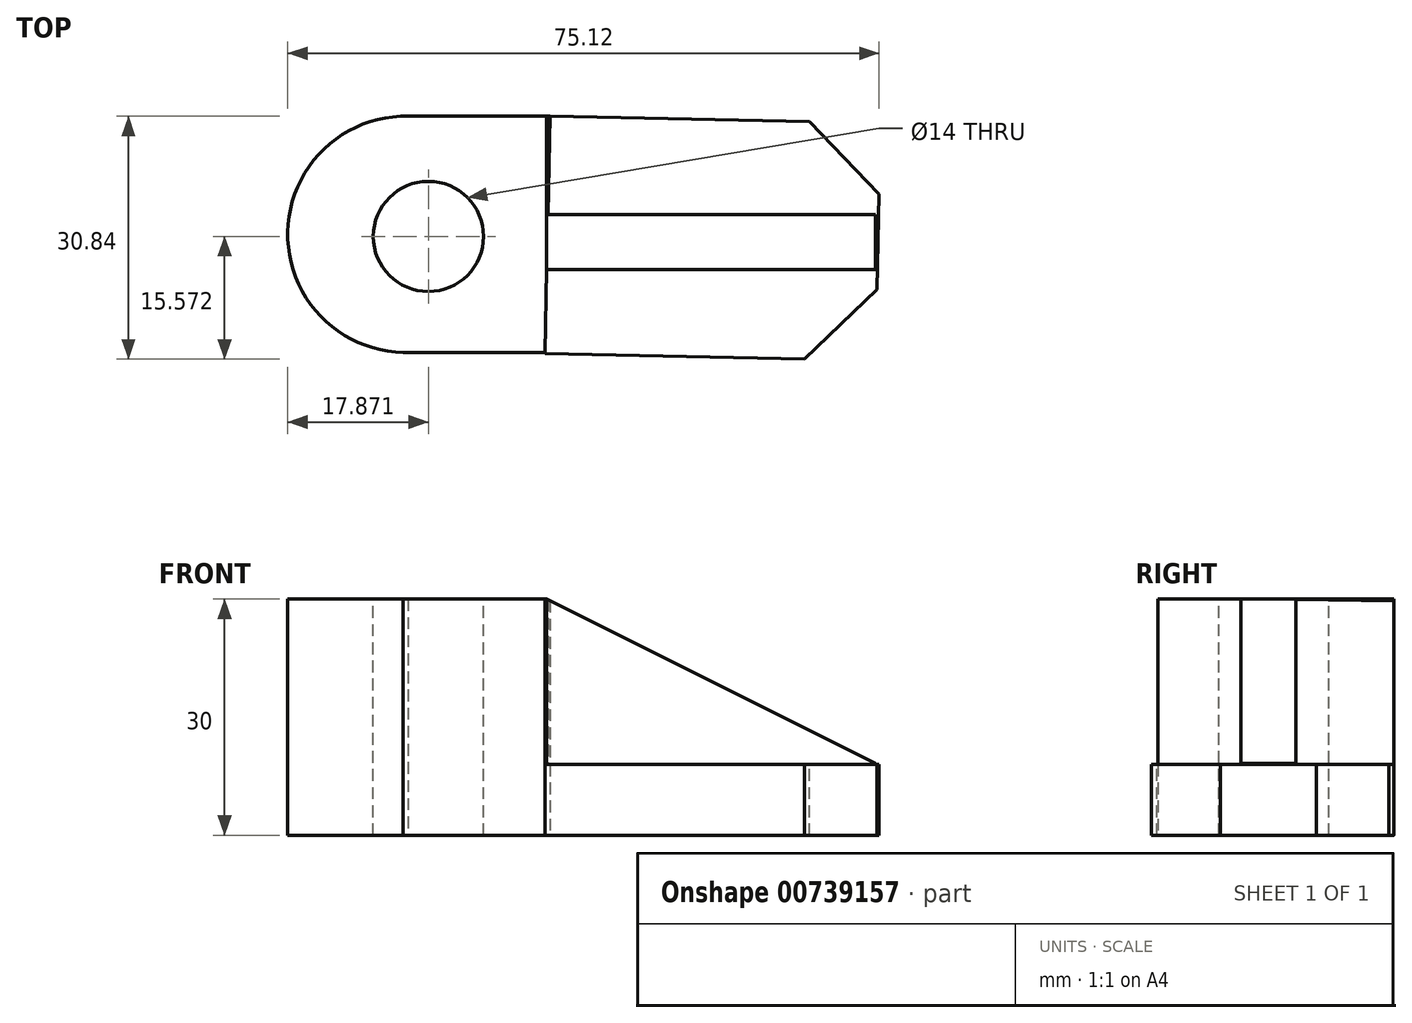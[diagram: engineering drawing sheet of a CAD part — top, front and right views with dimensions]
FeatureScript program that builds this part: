
annotation { "Feature Type Name" : "Feature", "Feature Type Description" : "" }
export const myFeature = defineFeature(function(context is Context, id is Id, definition is map)
    precondition{}
    {
        {
            var Q0;
            Q0=qCreatedBy(makeId("Top.planeOp"),FACE);
            var sketch = newSketch(context, id + "F0", { "sketchPlane" : qUnion([Q0])});
            skLineSegment(sketch, "E0", {"start": v(7.73, 30) * mm, "end": v(-10.27, 30) * mm});
            skLineSegment(sketch, "E1", {"start": v(7.1, 0) * mm, "end": v(-10.9, 0) * mm});
            skArc(sketch, "E2", {"start": v(-10.27, 30) * mm, "mid": v(-25.6, 15.32) * mm, "end": v(-10.9, 0) * mm});
            skLineSegment(sketch, "E3", {"start": v(7.73, 30) * mm, "end": v(7.1, 0) * mm});
            skSolve(sketch);
        }
        {
            var Q0;
            Q0 = qSketchRegion(id + "F0", true);
            extrude(context, id + "F1", {"entities" : qUnion([Q0]), "depth" : 30 * mm, "offsetDistance" : 25 * mm});
        }
        {
            var Q0;
            Q0=makeQuery(id+"F1.opExtrude","CAP_FACE",FACE,{"disambiguationData":[OSD([sQuery(id+"F0.wireOp",EDGE,"E0"),sQuery(id+"F0.wireOp",EDGE,"E1"),sQuery(id+"F0.wireOp",EDGE,"E2"),sQuery(id+"F0.wireOp",EDGE,"E3")])],"isStart":false});
            var sketch = newSketch(context, id + "F2", { "sketchPlane" : qUnion([Q0])});
            skCircle(sketch, "E4", {"center": v(-7.72, 14.73) * mm, "radius": 7 * mm});
            skSolve(sketch);
        }
        {
            var Q0;
            Q0 = qSketchRegion(id + "F2", true);
            extrude(context, id + "F3", {"entities" : qUnion([Q0]), "operationType" : NewBodyOperationType.REMOVE, "oppositeDirection" : true, "depth" : 30 * mm, "offsetDistance" : 25 * mm});
        }
        {
            var Q0;
            Q0=makeQuery(id+"F1.opExtrude","SWEPT_FACE",FACE,{"disambiguationData":[OSD([sQuery(id+"F0.wireOp",EDGE,"E3")])]});
            var sketch = newSketch(context, id + "F4", { "sketchPlane" : qUnion([Q0])});
            skLineSegment(sketch, "E5.bottom", {"start": v(0, 0) * mm, "end": v(30.16, 0) * mm});
            skLineSegment(sketch, "E5.top", {"start": v(0, 9) * mm, "end": v(30.16, 9) * mm});
            skLineSegment(sketch, "E5.left", {"start": v(0, 0) * mm, "end": v(0, 9) * mm});
            skLineSegment(sketch, "E5.right", {"start": v(30.16, 0) * mm, "end": v(30.16, 9) * mm});
            skSolve(sketch);
        }
        {
            var Q0;
            Q0 = qSketchRegion(id + "F4", true);
            extrude(context, id + "F5", {"entities" : qUnion([Q0]), "operationType" : NewBodyOperationType.ADD, "depth" : 42 * mm, "offsetDistance" : 25 * mm});
        }
        {
            var Q0;
            Q0=makeQuery(id+"F5.opExtrude","SWEPT_FACE",FACE,{"disambiguationData":[OSD([sQuery(id+"F4.wireOp",EDGE,"E5.top")])]});
            var sketch = newSketch(context, id + "F6", { "sketchPlane" : qUnion([Q0])});
            skLineSegment(sketch, "E6", {"start": v(49.72, 29.12) * mm, "end": v(49.53, 20.12) * mm});
            skLineSegment(sketch, "E7", {"start": v(49.08, -1.03) * mm, "end": v(49.27, 7.97) * mm});
            skLineSegment(sketch, "E8", {"start": v(49.27, 7.97) * mm, "end": v(49.53, 20.12) * mm});
            skLineSegment(sketch, "E9", {"start": v(49.08, -1.03) * mm, "end": v(40.08, -0.84) * mm});
            skLineSegment(sketch, "E10", {"start": v(49.72, 29.12) * mm, "end": v(40.72, 29.3) * mm});
            skLineSegment(sketch, "E11", {"start": v(49.27, 7.97) * mm, "end": v(40.08, -0.84) * mm});
            skLineSegment(sketch, "E12", {"start": v(49.53, 20.12) * mm, "end": v(40.72, 29.3) * mm});
            skSolve(sketch);
        }
        {
            var Q0;
            Q0 = qSketchRegion(id + "F6", true);
            extrude(context, id + "F7", {"entities" : qUnion([Q0]), "operationType" : NewBodyOperationType.REMOVE, "oppositeDirection" : true, "depth" : 25 * mm, "offsetDistance" : 25 * mm});
        }
        {
            var Q0;
            Q0=makeQuery(id+"F5.opExtrude","SWEPT_FACE",FACE,{"disambiguationData":[OSD([sQuery(id+"F4.wireOp",EDGE,"E5.top")])]});
            var sketch = newSketch(context, id + "F8", { "sketchPlane" : qUnion([Q0])});
            skLineSegment(sketch, "E13.bottom", {"start": v(49.47, 17.51) * mm, "end": v(7.32, 17.51) * mm});
            skLineSegment(sketch, "E13.top", {"start": v(49.47, 10.51) * mm, "end": v(7.32, 10.51) * mm});
            skLineSegment(sketch, "E13.left", {"start": v(49.47, 17.51) * mm, "end": v(49.47, 10.51) * mm});
            skLineSegment(sketch, "E13.right", {"start": v(7.32, 17.51) * mm, "end": v(7.32, 10.51) * mm});
            skSolve(sketch);
        }
        {
            var Q0;
            Q0 = qSketchRegion(id + "F8", true);
            extrude(context, id + "F9", {"entities" : qUnion([Q0]), "operationType" : NewBodyOperationType.ADD, "depth" : 21 * mm, "offsetDistance" : 25 * mm});
        }
        {
            var Q0;
            Q0=makeQuery(id+"F9.opExtrude","SWEPT_FACE",FACE,{"disambiguationData":[OSD([sQuery(id+"F8.wireOp",EDGE,"E13.top")])]});
            var sketch = newSketch(context, id + "F10", { "sketchPlane" : qUnion([Q0])});
            skLineSegment(sketch, "E14", {"start": v(7.32, 30) * mm, "end": v(49.32, 9) * mm});
            skLineSegment(sketch, "E15", {"start": v(49.32, 9) * mm, "end": v(49.47, 30) * mm});
            skLineSegment(sketch, "E16", {"start": v(49.47, 30) * mm, "end": v(7.32, 30) * mm});
            skSolve(sketch);
        }
        {
            var Q0;
            Q0 = qSketchRegion(id + "F10", true);
            extrude(context, id + "F11", {"entities" : qUnion([Q0]), "operationType" : NewBodyOperationType.REMOVE, "oppositeDirection" : true, "depth" : 25 * mm, "offsetDistance" : 25 * mm});
        }
        {
            var Q0;
            Q0=makeQuery(id+"F9.opExtrude","SWEPT_FACE",FACE,{"disambiguationData":[OSD([sQuery(id+"F8.wireOp",EDGE,"E13.left")])]});
            var sketch = newSketch(context, id + "F12", { "sketchPlane" : qUnion([Q0])});
            skLineSegment(sketch, "E17.bottom", {"start": v(17.51, 9) * mm, "end": v(10.51, 9) * mm});
            skLineSegment(sketch, "E17.top", {"start": v(17.51, 30) * mm, "end": v(10.51, 30) * mm});
            skLineSegment(sketch, "E17.left", {"start": v(17.51, 9) * mm, "end": v(17.51, 30) * mm});
            skLineSegment(sketch, "E17.right", {"start": v(10.51, 9) * mm, "end": v(10.51, 30) * mm});
            skSolve(sketch);
        }
        {
            var Q0;
            Q0 = qSketchRegion(id + "F12", true);
            extrude(context, id + "F13", {"entities" : qUnion([Q0]), "operationType" : NewBodyOperationType.REMOVE, "oppositeDirection" : true, "depth" : .4 * mm, "offsetDistance" : 25 * mm});
        }
    });
